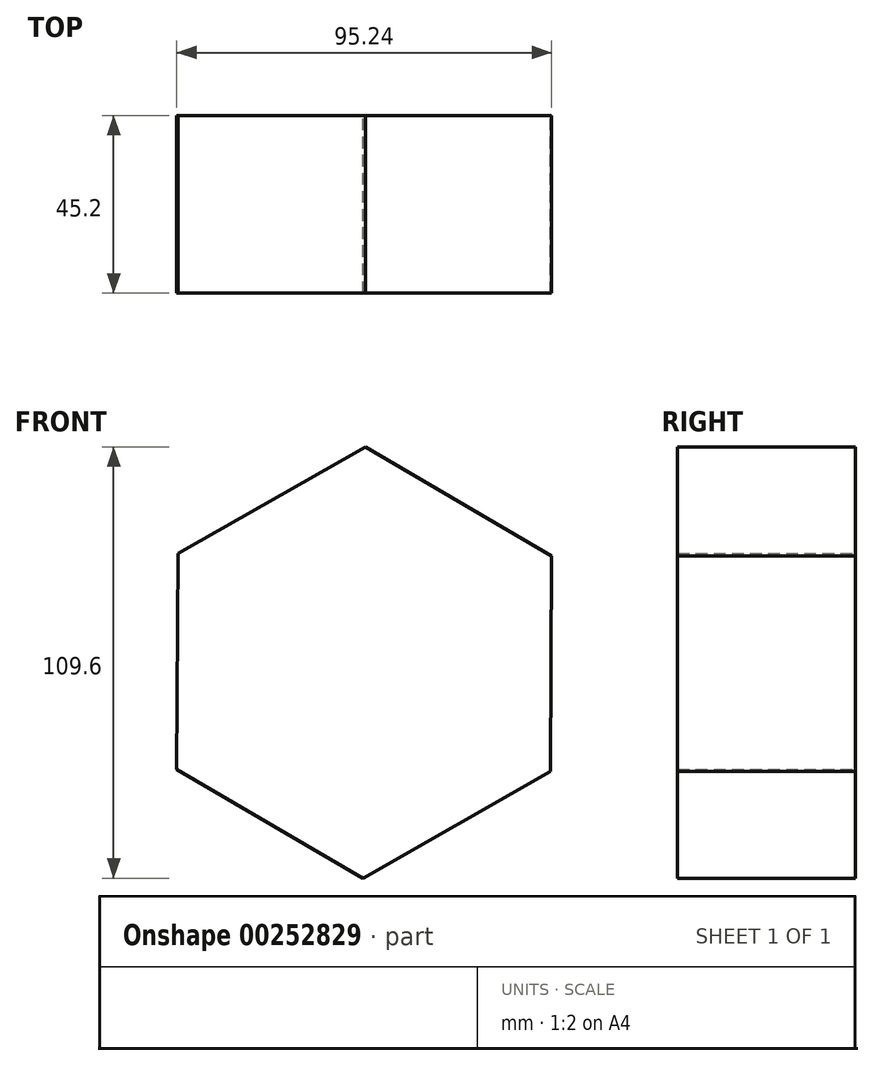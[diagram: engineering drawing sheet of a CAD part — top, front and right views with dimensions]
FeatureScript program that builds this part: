
annotation { "Feature Type Name" : "Feature", "Feature Type Description" : "" }
export const myFeature = defineFeature(function(context is Context, id is Id, definition is map)
    precondition{}
    {
        {
            var Q0;
            Q0=qCreatedBy(makeId("Front.planeOp"),FACE);
            var sketch = newSketch(context, id + "F0", { "sketchPlane" : qUnion([Q0])});
            skCircle(sketch, "E0.cCircle", {"center": v(0, 0) * mm, "radius": 54.8 * mm, "construction": true});
            skLineSegment(sketch, "E0.0", {"start": v(47.62, 27.11) * mm, "end": v(47.29, -27.69) * mm});
            skLineSegment(sketch, "E0.1", {"start": v(47.29, -27.69) * mm, "end": v(-0.33, -54.8) * mm});
            skLineSegment(sketch, "E0.2", {"start": v(-0.33, -54.8) * mm, "end": v(-47.62, -27.11) * mm});
            skLineSegment(sketch, "E0.3", {"start": v(-47.62, -27.11) * mm, "end": v(-47.29, 27.69) * mm});
            skLineSegment(sketch, "E0.4", {"start": v(-47.29, 27.69) * mm, "end": v(0.33, 54.8) * mm});
            skLineSegment(sketch, "E0.5", {"start": v(0.33, 54.8) * mm, "end": v(47.62, 27.11) * mm});
            skSolve(sketch);
        }
        {
            var Q0;
            Q0 = qSketchRegion(id + "F0", true);
            extrude(context, id + "F1", {"entities" : qUnion([Q0]), "endBound" : BoundingType.SYMMETRIC, "depth" : 45.2 * mm});
        }
    });
